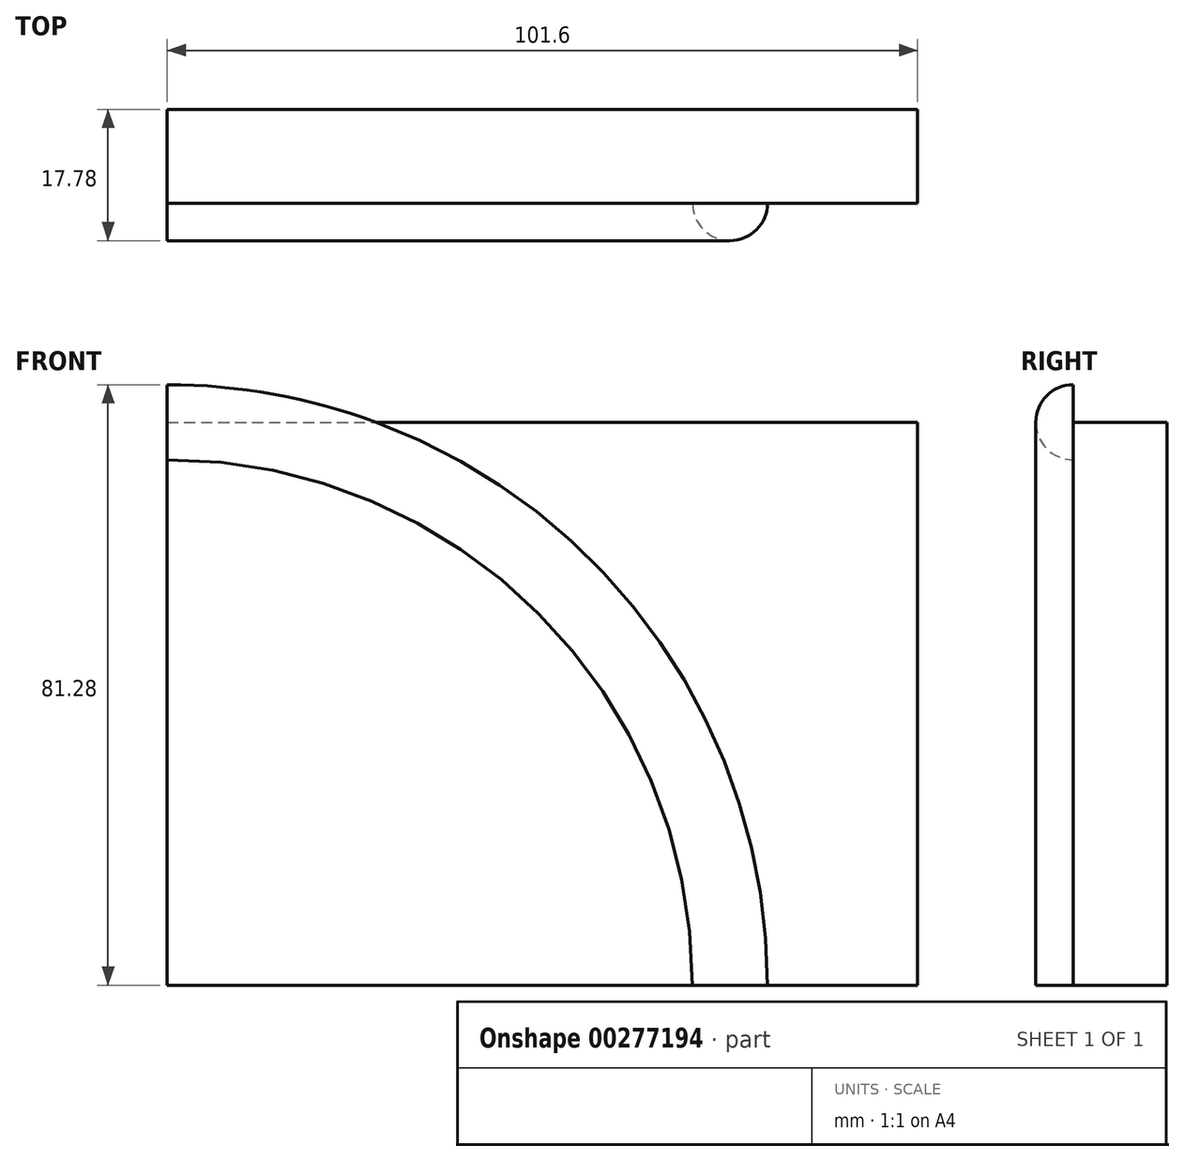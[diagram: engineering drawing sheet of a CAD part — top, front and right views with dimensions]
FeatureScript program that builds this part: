
annotation { "Feature Type Name" : "Feature", "Feature Type Description" : "" }
export const myFeature = defineFeature(function(context is Context, id is Id, definition is map)
    precondition{}
    {
        {
            var Q0;
            Q0=qCreatedBy(makeId("Front.planeOp"),FACE);
            var sketch = newSketch(context, id + "F0", { "sketchPlane" : qUnion([Q0])});
            skLineSegment(sketch, "E0.bottom", {"start": v(0, 0) * mm, "end": v(101.6, 0) * mm});
            skLineSegment(sketch, "E0.top", {"start": v(0, 76.2) * mm, "end": v(101.6, 76.2) * mm});
            skLineSegment(sketch, "E0.left", {"start": v(0, 0) * mm, "end": v(0, 76.2) * mm});
            skLineSegment(sketch, "E0.right", {"start": v(101.6, 0) * mm, "end": v(101.6, 76.2) * mm});
            skArc(sketch, "E1", {"start": v(0, 76.2) * mm, "mid": v(53.88, 53.88) * mm, "end": v(76.2, 0) * mm});
            skSolve(sketch);
        }
        {
            var Q0;
            Q0 = qSketchRegion(id + "F0", true);
            extrude(context, id + "F1", {"entities" : qUnion([Q0]), "depth" : 12.7 * mm});
        }
        {
            var Q0;
            Q0=qCreatedBy(makeId("Top.planeOp"),FACE);
            var sketch = newSketch(context, id + "F2", { "sketchPlane" : qUnion([Q0])});
            skLineSegment(sketch, "E2", {"start": v(0, 0) * mm, "end": v(76.2, 0) * mm});
            skLineSegment(sketch, "E3", {"start": v(76.2, 0) * mm, "end": v(76.2, -12.7) * mm});
            skArc(sketch, "E4", {"start": v(71.12, -12.7) * mm, "mid": v(76.2, -17.78) * mm, "end": v(81.28, -12.7) * mm});
            skLineSegment(sketch, "E5", {"start": v(71.12, -12.7) * mm, "end": v(81.28, -12.7) * mm});
            skSolve(sketch);
        }
        {
            var Q0;
            {var subQ0=sQuery(id+"F2.wireOp",EDGE,"E4");Q0=makeQuery(id+"F2.imprint","IMPRINT",FACE,{"disambiguationData":[TD([[makeQuery(id+"F2.imprint","IMPRINT",EDGE,{"derivedFrom":subQ0}),1.0]])]});}
            var Q1;
            Q1=sQuery(id+"F0.wireOp",EDGE,"E1");
            sweep(context, id + "F3", {"operationType" : NewBodyOperationType.ADD, "profiles" : qUnion([Q0]), "path" : qUnion([Q1])});
        }
    });
